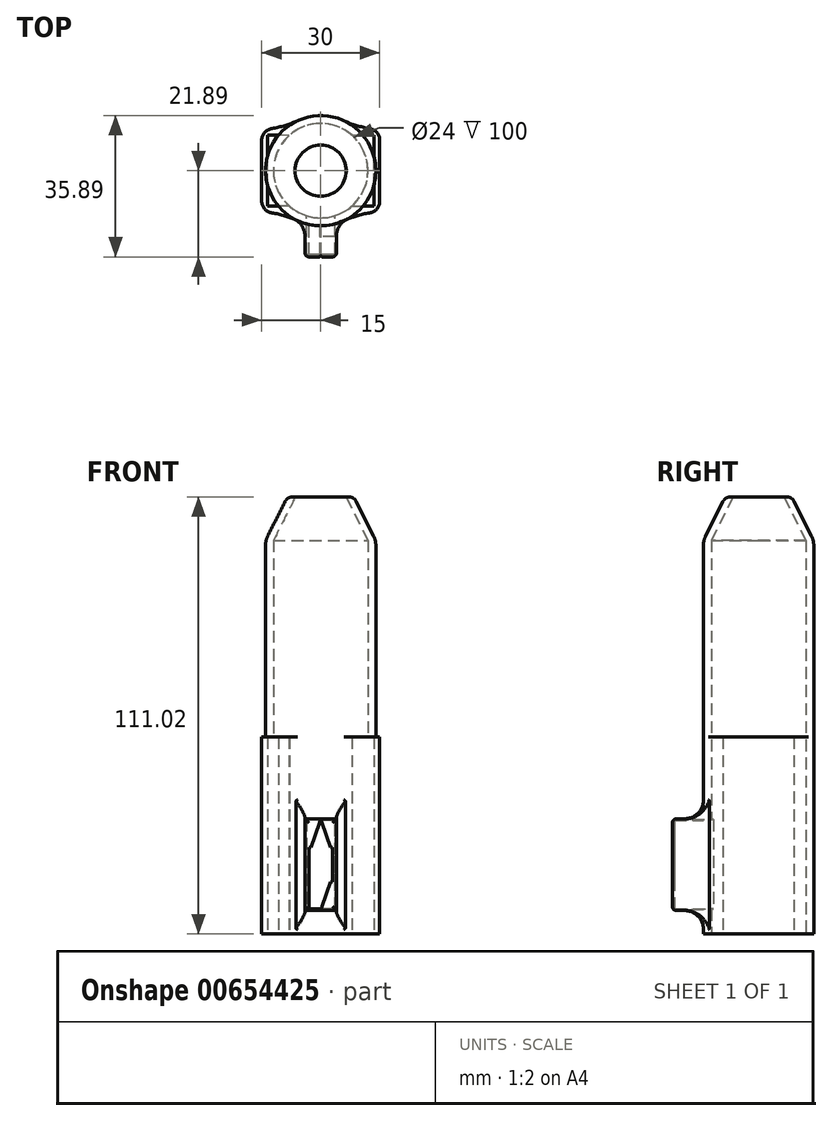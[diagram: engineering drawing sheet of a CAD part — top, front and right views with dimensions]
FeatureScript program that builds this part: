
annotation { "Feature Type Name" : "Feature", "Feature Type Description" : "" }
export const myFeature = defineFeature(function(context is Context, id is Id, definition is map)
    precondition{}
    {
        {
            var Q0;
            Q0=qCreatedBy(makeId("Front.planeOp"),FACE);
            var sketch = newSketch(context, id + "F0", { "sketchPlane" : qUnion([Q0])});
            skLineSegment(sketch, "E0", {"start": v(-12, -57.81) * mm, "end": v(-12, 40.19) * mm});
            skLineSegment(sketch, "E1", {"start": v(-12, 40.19) * mm, "end": v(-14, 40.19) * mm});
            skLineSegment(sketch, "E2", {"start": v(-14, 40.19) * mm, "end": v(-14, -59.81) * mm});
            skLineSegment(sketch, "E3", {"start": v(0, -59.81) * mm, "end": v(0, -57.81) * mm});
            skLineSegment(sketch, "E4", {"start": v(-12, 40.19) * mm, "end": v(-6.5, 51.08) * mm});
            skLineSegment(sketch, "E5", {"start": v(-14, 40.19) * mm, "end": v(-6.5, 55.08) * mm});
            skLineSegment(sketch, "E6", {"start": v(-6.5, 55.08) * mm, "end": v(-6.5, 51.08) * mm});
            skLineSegment(sketch, "E7", {"start": v(-12, -57.81) * mm, "end": v(-12, -59.81) * mm});
            skLineSegment(sketch, "E8", {"start": v(-12, -59.81) * mm, "end": v(-14, -59.81) * mm});
            skSolve(sketch);
        }
        {
            var Q0;
            Q0 = qSketchRegion(id + "F0", true);
            var Q1;
            Q1=sQuery(id+"F0.wireOp",EDGE,"E3");
            revolve(context, id + "F1", {"entities" : qUnion([Q0]), "axis" : qUnion([Q1]), "revolveType" : RevolveType.FULL});
        }
        {
            var Q0;
            Q0=makeQuery(id+"F1.opRevolve","SWEPT_EDGE",EDGE,{"disambiguationData":[OSD([sQuery(id+"F0.wireOp",EDGE,"E5"),sQuery(id+"F0.wireOp",EDGE,"E6")])]});
            fillet(context, id + "F2", {"entities" : qUnion([Q0]), "radius" : 2 * mm, "tangentPropagation" : true, "allowEdgeOverflow" : false});
        }
        {
            var Q0;
            Q0=makeQuery(id+"F1.opRevolve","SWEPT_EDGE",EDGE,{"disambiguationData":[OSD([sQuery(id+"F0.wireOp",EDGE,"E1"),sQuery(id+"F0.wireOp",EDGE,"E2"),sQuery(id+"F0.wireOp",EDGE,"E5")])]});
            fillet(context, id + "F3", {"entities" : qUnion([Q0]), "radius" : 5 * mm, "tangentPropagation" : true, "allowEdgeOverflow" : false});
        }
        {
            var Q0;
            Q0=qCreatedBy(makeId("Front.planeOp"),FACE);
            var sketch = newSketch(context, id + "F4", { "sketchPlane" : qUnion([Q0])});
            skLineSegment(sketch, "E9.bottom", {"start": v(4, -30.57) * mm, "end": v(-4, -30.57) * mm});
            skLineSegment(sketch, "E9.top", {"start": v(4, -53.87) * mm, "end": v(-4, -53.87) * mm});
            skLineSegment(sketch, "E9.left", {"start": v(4, -30.57) * mm, "end": v(4, -53.87) * mm});
            skLineSegment(sketch, "E9.right", {"start": v(-4, -30.57) * mm, "end": v(-4, -53.87) * mm});
            skLineSegment(sketch, "E10", {"start": v(-4, -30.57) * mm, "end": v(-3, -30.57) * mm});
            skLineSegment(sketch, "E11", {"start": v(4, -30.57) * mm, "end": v(3, -30.57) * mm});
            skLineSegment(sketch, "E12", {"start": v(3, -30.57) * mm, "end": v(3, -53.87) * mm});
            skLineSegment(sketch, "E13", {"start": v(-3, -30.57) * mm, "end": v(-3, -53.87) * mm});
            skLineSegment(sketch, "E14", {"start": v(0, -30.57) * mm, "end": v(-2.5, -37.87) * mm});
            skLineSegment(sketch, "E15", {"start": v(-2.5, -37.87) * mm, "end": v(-3, -37.87) * mm});
            skLineSegment(sketch, "E16", {"start": v(3, -37.87) * mm, "end": v(2.5, -37.87) * mm});
            skLineSegment(sketch, "E17", {"start": v(0, -30.57) * mm, "end": v(2.5, -37.87) * mm});
            skLineSegment(sketch, "E18", {"start": v(3, -46.57) * mm, "end": v(2.5, -46.57) * mm});
            skLineSegment(sketch, "E19", {"start": v(2.5, -46.57) * mm, "end": v(0, -53.87) * mm});
            skLineSegment(sketch, "E20", {"start": v(-3, -46.57) * mm, "end": v(-2.5, -46.57) * mm});
            skLineSegment(sketch, "E21", {"start": v(-2.5, -46.57) * mm, "end": v(0, -53.87) * mm});
            skLineSegment(sketch, "E22", {"start": v(-2.5, -46.57) * mm, "end": v(-3, -46.57) * mm});
            skLineSegment(sketch, "E23", {"start": v(-0.12, -30.9) * mm, "end": v(0, -30.87) * mm});
            skLineSegment(sketch, "E24", {"start": v(-0.1, -53.56) * mm, "end": v(0.14, -53.47) * mm});
            skLineSegment(sketch, "E25", {"start": v(-3, -30.84) * mm, "end": v(3, -30.84) * mm});
            skLineSegment(sketch, "E26", {"start": v(-3, -53.57) * mm, "end": v(3, -53.57) * mm});
            skSolve(sketch);
        }
        {
            var Q0;
            Q0 = qSketchRegion(id + "F4", true);
            var Q1;
            {var subQ4=sQuery(id+"F4.wireOp",EDGE,"E18");Q1=makeQuery(id+"F4.imprint","IMPRINT",FACE,{"disambiguationData":[TD([[makeQuery(id+"F4.imprint","IMPRINT",EDGE,{"derivedFrom":subQ4}),1.0]])]});}
            var Q2;
            {var subQ0=sQuery(id+"F4.wireOp",EDGE,"E22");Q2=makeQuery(id+"F4.imprint","IMPRINT",FACE,{"disambiguationData":[TD([[makeQuery(id+"F4.imprint","IMPRINT",EDGE,{"derivedFrom":subQ0}),1.0]])]});}
            var Q3;
            {var subQ0=sQuery(id+"F4.wireOp",EDGE,"E15");Q3=makeQuery(id+"F4.imprint","IMPRINT",FACE,{"disambiguationData":[TD([[makeQuery(id+"F4.imprint","IMPRINT",EDGE,{"derivedFrom":subQ0}),-1.0]])]});}
            var Q4;
            {var subQ0=sQuery(id+"F4.wireOp",EDGE,"E16");Q4=makeQuery(id+"F4.imprint","IMPRINT",FACE,{"disambiguationData":[TD([[makeQuery(id+"F4.imprint","IMPRINT",EDGE,{"derivedFrom":subQ0}),-1.0]])]});}
            extrude(context, id + "F5", {"entities" : qUnion([Q0, Q1, Q2, Q3, Q4]), "operationType" : NewBodyOperationType.ADD, "depth" : 17.79 * mm, "offsetDistance" : 25 * mm});
        }
        {
            var Q0;
            Q0=makeQuery(id+"F5.opExtrude","CAP_FACE",FACE,{"disambiguationData":[OSD([sQuery(id+"F4.wireOp",EDGE,"E9.bottom"),sQuery(id+"F4.wireOp",EDGE,"E9.top"),sQuery(id+"F4.wireOp",EDGE,"E9.left"),sQuery(id+"F4.wireOp",EDGE,"E9.right"),sQuery(id+"F4.wireOp",EDGE,"E10"),sQuery(id+"F4.wireOp",EDGE,"E11"),sQuery(id+"F4.wireOp",EDGE,"E12"),sQuery(id+"F4.wireOp",EDGE,"E13"),sQuery(id+"F4.wireOp",EDGE,"E14"),sQuery(id+"F4.wireOp",EDGE,"E15"),sQuery(id+"F4.wireOp",EDGE,"E16"),sQuery(id+"F4.wireOp",EDGE,"E17"),sQuery(id+"F4.wireOp",EDGE,"E18"),sQuery(id+"F4.wireOp",EDGE,"E19"),sQuery(id+"F4.wireOp",EDGE,"E21"),sQuery(id+"F4.wireOp",EDGE,"E22"),sQuery(id+"F4.wireOp",EDGE,"E25"),sQuery(id+"F4.wireOp",EDGE,"E26")])],"isStart":true});
            var sketch = newSketch(context, id + "F6", { "sketchPlane" : qUnion([Q0])});
            skSolve(sketch);
        }
        {
            var Q0;
            Q0=makeQuery(id+"F6.imprint","IMPRINT",FACE,{"disambiguationData":[TD([[makeQuery(id+"F6.imprint","IMPRINT",EDGE,{"derivedFrom":makeQuery(id+"F5.opExtrude","CAP_EDGE",EDGE,{"disambiguationData":[OSD([sQuery(id+"F4.wireOp",EDGE,"E9.top")])],"isStart":true})}),1.0]])]});
            var sketch = newSketch(context, id + "F7", { "sketchPlane" : qUnion([Q0])});
            skLineSegment(sketch, "E27.bottom", {"start": v(-3.6, -53.47) * mm, "end": v(3.6, -53.47) * mm});
            skLineSegment(sketch, "E27.top", {"start": v(-3.6, -30.97) * mm, "end": v(3.6, -30.97) * mm});
            skLineSegment(sketch, "E27.left", {"start": v(-3.6, -53.47) * mm, "end": v(-3.6, -30.97) * mm});
            skLineSegment(sketch, "E27.right", {"start": v(3.6, -53.47) * mm, "end": v(3.6, -30.97) * mm});
            skSolve(sketch);
        }
        {
            var Q0;
            Q0 = qSketchRegion(id + "F7", true);
            extrude(context, id + "F8", {"entities" : qUnion([Q0]), "operationType" : NewBodyOperationType.REMOVE, "oppositeDirection" : true, "depth" : 16.7 * mm, "offsetDistance" : 25 * mm});
        }
        {
            var Q0;
            {var subQ2=sQuery(id+"F4.wireOp",EDGE,"E9.top");Q0=makeQuery(id+"F5.boolean.opBoolean","SPLIT",FACE,{"disambiguationData":[TD([makeQuery(id+"F1.opRevolve","SWEPT_FACE",FACE,{"disambiguationData":[OSD([sQuery(id+"F0.wireOp",EDGE,"E0"),sQuery(id+"F0.wireOp",EDGE,"E7")])]})])],"derivedFrom":makeQuery(id+"F5.opExtrude","SWEPT_FACE",FACE,{"disambiguationData":[OSD([subQ2])]})});}
            extrude(context, id + "F9", {"entities" : qUnion([Q0]), "operationType" : NewBodyOperationType.REMOVE, "oppositeDirection" : true, "depth" : 25 * mm, "offsetDistance" : 25 * mm});
        }
        {
            var Q0;
            {var subQ0=sQuery(id+"F7.wireOp",EDGE,"E27.left");var subQ1=sQuery(id+"F7.wireOp",EDGE,"E27.bottom");var subQ2=sQuery(id+"F7.wireOp",EDGE,"E27.top");Q0=makeQuery(id+"F8.boolean.opBoolean","COPY",FACE,{"disambiguationData":[TD([makeQuery(id+"F5.opExtrude","SWEPT_FACE",FACE,{"disambiguationData":[OSD([sQuery(id+"F4.wireOp",EDGE,"E12")])]})])],"derivedFrom":makeQuery(id+"F8.opExtrude","CAP_FACE",FACE,{"disambiguationData":[OSD([subQ1,subQ2,subQ0,sQuery(id+"F7.wireOp",EDGE,"E27.right")])],"isStart":false})});}
            var sketch = newSketch(context, id + "F10", { "sketchPlane" : qUnion([Q0])});
            skLineSegment(sketch, "E28", {"start": v(-3.6, -53.47) * mm, "end": v(-3.6, -30.97) * mm});
            skSolve(sketch);
        }
        {
            var Q0;
            Q0=makeQuery(id+"F8.boolean.opBoolean","COPY",FACE,{"derivedFrom":makeQuery(id+"F8.opExtrude","SWEPT_FACE",FACE,{"disambiguationData":[OSD([sQuery(id+"F7.wireOp",EDGE,"E27.top")])]})});
            extrude(context, id + "F11", {"entities" : qUnion([Q0]), "operationType" : NewBodyOperationType.REMOVE, "oppositeDirection" : true, "depth" : 0.19 * mm, "offsetDistance" : 25 * mm});
        }
        {
            var Q0;
            Q0=makeQuery(id+"F1.opRevolve","SWEPT_FACE",FACE,{"disambiguationData":[OSD([sQuery(id+"F0.wireOp",EDGE,"E8")])]});
            var sketch = newSketch(context, id + "F12", { "sketchPlane" : qUnion([Q0])});
            skLineSegment(sketch, "E29", {"start": v(13.5, 0) * mm, "end": v(13.5, -9) * mm});
            skLineSegment(sketch, "E30", {"start": v(13.5, 0) * mm, "end": v(13.5, 9) * mm});
            skLineSegment(sketch, "E31", {"start": v(-13.5, 9) * mm, "end": v(-13.5, 0) * mm});
            skLineSegment(sketch, "E32", {"start": v(-13.5, -9) * mm, "end": v(-13.5, 0) * mm});
            skLineSegment(sketch, "E33", {"start": v(13.5, 9) * mm, "end": v(15, 9) * mm});
            skLineSegment(sketch, "E34", {"start": v(13.5, -9) * mm, "end": v(15, -9) * mm});
            skLineSegment(sketch, "E35", {"start": v(15, 9) * mm, "end": v(15, -9) * mm});
            skLineSegment(sketch, "E36", {"start": v(13.5, 9) * mm, "end": v(13.5, 10.5) * mm});
            skLineSegment(sketch, "E37", {"start": v(13.5, -9) * mm, "end": v(13.5, -10.5) * mm});
            skLineSegment(sketch, "E38", {"start": v(-13.5, -9) * mm, "end": v(-13.5, -10.5) * mm});
            skLineSegment(sketch, "E39", {"start": v(-13.5, -9) * mm, "end": v(-15, -9) * mm});
            skLineSegment(sketch, "E40", {"start": v(-14, 0) * mm, "end": v(-13.5, 0) * mm});
            skLineSegment(sketch, "E41", {"start": v(13.5, 0) * mm, "end": v(14, 0) * mm});
            skLineSegment(sketch, "E42", {"start": v(-13.5, 9) * mm, "end": v(-13.5, 10.5) * mm});
            skLineSegment(sketch, "E43", {"start": v(-13.5, 9) * mm, "end": v(-15, 9) * mm});
            skLineSegment(sketch, "E44", {"start": v(-15, 9) * mm, "end": v(-15, -10.5) * mm});
            skLineSegment(sketch, "E45", {"start": v(15, -10.5) * mm, "end": v(15, 10.5) * mm});
            skLineSegment(sketch, "E46", {"start": v(-15, 9) * mm, "end": v(-15, 10.5) * mm});
            skLineSegment(sketch, "E47", {"start": v(-15, 10.5) * mm, "end": v(-13.5, 10.5) * mm});
            skLineSegment(sketch, "E48", {"start": v(9.56, 9) * mm, "end": v(7.85, 10.5) * mm});
            skLineSegment(sketch, "E49", {"start": v(-7.61, 10.5) * mm, "end": v(-9.13, 9) * mm});
            skLineSegment(sketch, "E50", {"start": v(-9.13, 9) * mm, "end": v(-13.5, 9) * mm});
            skLineSegment(sketch, "E51", {"start": v(9.56, 9) * mm, "end": v(13.5, 9) * mm});
            skLineSegment(sketch, "E52", {"start": v(7.85, 10.5) * mm, "end": v(13.5, 10.5) * mm});
            skLineSegment(sketch, "E53", {"start": v(-7.61, 10.5) * mm, "end": v(-13.5, 10.5) * mm});
            skLineSegment(sketch, "E54", {"start": v(13.5, 10.5) * mm, "end": v(15, 10.5) * mm});
            skLineSegment(sketch, "E55", {"start": v(-7.73, -10.5) * mm, "end": v(-8.96, -9) * mm});
            skLineSegment(sketch, "E56", {"start": v(9.29, -9) * mm, "end": v(7.83, -10.5) * mm});
            skLineSegment(sketch, "E57", {"start": v(7.83, -10.5) * mm, "end": v(15, -10.5) * mm});
            skLineSegment(sketch, "E58", {"start": v(-7.73, -10.5) * mm, "end": v(-15, -10.5) * mm});
            skLineSegment(sketch, "E59", {"start": v(9.29, -9) * mm, "end": v(13.5, -9) * mm});
            skLineSegment(sketch, "E60", {"start": v(-8.96, -9) * mm, "end": v(-13.5, -9) * mm});
            skSolve(sketch);
        }
        {
            var Q0;
            Q0 = qSketchRegion(id + "F12", true);
            extrude(context, id + "F13", {"entities" : qUnion([Q0]), "operationType" : NewBodyOperationType.ADD, "oppositeDirection" : true, "depth" : 50 * mm, "offsetDistance" : 25 * mm});
        }
        {
            var Q0;
            Q0=makeQuery(id+"F13.boolean.opBoolean","MERGE",FACE,{"derivedFrom":[makeQuery(id+"F1.opRevolve","SWEPT_FACE",FACE,{"disambiguationData":[OSD([sQuery(id+"F0.wireOp",EDGE,"E8")])]}),makeQuery(id+"F13.opExtrude","CAP_FACE",FACE,{"disambiguationData":[OSD([sQuery(id+"F12.wireOp",EDGE,"E29"),sQuery(id+"F12.wireOp",EDGE,"E30"),sQuery(id+"F12.wireOp",EDGE,"E45"),sQuery(id+"F12.wireOp",EDGE,"E48"),sQuery(id+"F12.wireOp",EDGE,"E51"),sQuery(id+"F12.wireOp",EDGE,"E52"),sQuery(id+"F12.wireOp",EDGE,"E54"),sQuery(id+"F12.wireOp",EDGE,"E56"),sQuery(id+"F12.wireOp",EDGE,"E57"),sQuery(id+"F12.wireOp",EDGE,"E59")])],"isStart":true}),makeQuery(id+"F13.opExtrude","CAP_FACE",FACE,{"disambiguationData":[OSD([sQuery(id+"F12.wireOp",EDGE,"E31"),sQuery(id+"F12.wireOp",EDGE,"E32"),sQuery(id+"F12.wireOp",EDGE,"E44"),sQuery(id+"F12.wireOp",EDGE,"E46"),sQuery(id+"F12.wireOp",EDGE,"E47"),sQuery(id+"F12.wireOp",EDGE,"E49"),sQuery(id+"F12.wireOp",EDGE,"E50"),sQuery(id+"F12.wireOp",EDGE,"E53"),sQuery(id+"F12.wireOp",EDGE,"E55"),sQuery(id+"F12.wireOp",EDGE,"E58"),sQuery(id+"F12.wireOp",EDGE,"E60")])],"isStart":true})]});
            var sketch = newSketch(context, id + "F14", { "sketchPlane" : qUnion([Q0])});
            skLineSegment(sketch, "E61", {"start": v(10.72, 9) * mm, "end": v(7.94, 9) * mm});
            skLineSegment(sketch, "E62", {"start": v(7.94, 9) * mm, "end": v(7.94, 3.7) * mm});
            skLineSegment(sketch, "E63", {"start": v(7.94, 3.7) * mm, "end": v(13.5, 3.7) * mm});
            skLineSegment(sketch, "E64", {"start": v(13.5, -3.7) * mm, "end": v(8.05, -3.7) * mm});
            skLineSegment(sketch, "E65", {"start": v(8.05, -3.7) * mm, "end": v(7.49, -3.7) * mm});
            skLineSegment(sketch, "E66", {"start": v(7.49, -3.7) * mm, "end": v(7.49, -9) * mm});
            skLineSegment(sketch, "E67", {"start": v(7.49, -9) * mm, "end": v(10.72, -9) * mm});
            skLineSegment(sketch, "E68", {"start": v(-13.5, -3.7) * mm, "end": v(-6.61, -3.7) * mm});
            skLineSegment(sketch, "E69", {"start": v(-6.61, -3.7) * mm, "end": v(-6.61, -8.93) * mm});
            skLineSegment(sketch, "E70", {"start": v(-6.61, -8.93) * mm, "end": v(-10.72, -9) * mm});
            skLineSegment(sketch, "E71", {"start": v(-10.72, -9) * mm, "end": v(-13.5, -9) * mm});
            skLineSegment(sketch, "E72", {"start": v(-13.5, -9) * mm, "end": v(-13.5, -3.7) * mm});
            skLineSegment(sketch, "E73", {"start": v(10.72, -9) * mm, "end": v(13.5, -9) * mm});
            skLineSegment(sketch, "E74", {"start": v(13.5, -9) * mm, "end": v(13.5, -3.7) * mm});
            skLineSegment(sketch, "E75", {"start": v(10.72, 9) * mm, "end": v(13.5, 9) * mm});
            skLineSegment(sketch, "E76", {"start": v(13.5, 9) * mm, "end": v(13.5, 3.7) * mm});
            skLineSegment(sketch, "E77", {"start": v(-13.5, 9) * mm, "end": v(-4.7, 9) * mm});
            skLineSegment(sketch, "E78", {"start": v(-4.7, 9) * mm, "end": v(-4.6, 3.7) * mm});
            skLineSegment(sketch, "E79", {"start": v(-4.6, 3.7) * mm, "end": v(-13.5, 3.7) * mm});
            skLineSegment(sketch, "E80", {"start": v(-13.5, 3.7) * mm, "end": v(-13.5, 9) * mm});
            skSolve(sketch);
        }
        {
            var Q0;
            Q0 = qSketchRegion(id + "F14", true);
            extrude(context, id + "F15", {"entities" : qUnion([Q0]), "operationType" : NewBodyOperationType.REMOVE, "oppositeDirection" : true, "depth" : 50 * mm, "offsetDistance" : 25 * mm});
        }
        {
            var Q0;
            Q0=makeQuery(id+"F13.boolean.opBoolean","MERGE",FACE,{"derivedFrom":[makeQuery(id+"F1.opRevolve","SWEPT_FACE",FACE,{"disambiguationData":[OSD([sQuery(id+"F0.wireOp",EDGE,"E8")])]}),makeQuery(id+"F13.opExtrude","CAP_FACE",FACE,{"disambiguationData":[OSD([sQuery(id+"F12.wireOp",EDGE,"E29"),sQuery(id+"F12.wireOp",EDGE,"E30"),sQuery(id+"F12.wireOp",EDGE,"E45"),sQuery(id+"F12.wireOp",EDGE,"E48"),sQuery(id+"F12.wireOp",EDGE,"E51"),sQuery(id+"F12.wireOp",EDGE,"E52"),sQuery(id+"F12.wireOp",EDGE,"E54"),sQuery(id+"F12.wireOp",EDGE,"E56"),sQuery(id+"F12.wireOp",EDGE,"E57"),sQuery(id+"F12.wireOp",EDGE,"E59")])],"isStart":true}),makeQuery(id+"F13.opExtrude","CAP_FACE",FACE,{"disambiguationData":[OSD([sQuery(id+"F12.wireOp",EDGE,"E31"),sQuery(id+"F12.wireOp",EDGE,"E32"),sQuery(id+"F12.wireOp",EDGE,"E44"),sQuery(id+"F12.wireOp",EDGE,"E46"),sQuery(id+"F12.wireOp",EDGE,"E47"),sQuery(id+"F12.wireOp",EDGE,"E49"),sQuery(id+"F12.wireOp",EDGE,"E50"),sQuery(id+"F12.wireOp",EDGE,"E53"),sQuery(id+"F12.wireOp",EDGE,"E55"),sQuery(id+"F12.wireOp",EDGE,"E58"),sQuery(id+"F12.wireOp",EDGE,"E60")])],"isStart":true})]});
            var sketch = newSketch(context, id + "F16", { "sketchPlane" : qUnion([Q0])});
            skLineSegment(sketch, "E81", {"start": v(13.5, 3.7) * mm, "end": v(13.5, -3.7) * mm});
            skLineSegment(sketch, "E82", {"start": v(13.5, -3.7) * mm, "end": v(8.2, -3.7) * mm});
            skLineSegment(sketch, "E83", {"start": v(8.2, -3.7) * mm, "end": v(8.2, 3.7) * mm});
            skLineSegment(sketch, "E84", {"start": v(8.2, 3.7) * mm, "end": v(13.5, 3.7) * mm});
            skLineSegment(sketch, "E85", {"start": v(-13.5, 3.7) * mm, "end": v(-13.5, -3.7) * mm});
            skLineSegment(sketch, "E86", {"start": v(-13.5, -3.7) * mm, "end": v(-6.7, -3.7) * mm});
            skLineSegment(sketch, "E87", {"start": v(-6.7, -3.7) * mm, "end": v(-6.7, 3.7) * mm});
            skLineSegment(sketch, "E88", {"start": v(-6.7, 3.7) * mm, "end": v(-13.5, 3.7) * mm});
            skSolve(sketch);
        }
        {
            var Q0;
            Q0 = qSketchRegion(id + "F16", true);
            extrude(context, id + "F17", {"entities" : qUnion([Q0]), "operationType" : NewBodyOperationType.REMOVE, "oppositeDirection" : true, "depth" : 50 * mm, "offsetDistance" : 25 * mm});
        }
        {
            var Q0;
            Q0=makeQuery(id+"F5.opExtrude","CAP_FACE",FACE,{"disambiguationData":[OSD([sQuery(id+"F4.wireOp",EDGE,"E9.bottom"),sQuery(id+"F4.wireOp",EDGE,"E9.top"),sQuery(id+"F4.wireOp",EDGE,"E9.left"),sQuery(id+"F4.wireOp",EDGE,"E9.right"),sQuery(id+"F4.wireOp",EDGE,"E10"),sQuery(id+"F4.wireOp",EDGE,"E11"),sQuery(id+"F4.wireOp",EDGE,"E12"),sQuery(id+"F4.wireOp",EDGE,"E13"),sQuery(id+"F4.wireOp",EDGE,"E14"),sQuery(id+"F4.wireOp",EDGE,"E15"),sQuery(id+"F4.wireOp",EDGE,"E16"),sQuery(id+"F4.wireOp",EDGE,"E17"),sQuery(id+"F4.wireOp",EDGE,"E18"),sQuery(id+"F4.wireOp",EDGE,"E19"),sQuery(id+"F4.wireOp",EDGE,"E21"),sQuery(id+"F4.wireOp",EDGE,"E22"),sQuery(id+"F4.wireOp",EDGE,"E25"),sQuery(id+"F4.wireOp",EDGE,"E26")])],"isStart":false});
            extrude(context, id + "F18", {"entities" : qUnion([Q0]), "operationType" : NewBodyOperationType.ADD, "depth" : 4.1 * mm, "offsetDistance" : 25 * mm});
        }
        {
            var Q0;
            Q0=makeQuery(id+"F10.imprint","IMPRINT",FACE,{"disambiguationData":[TD([[makeQuery(id+"F10.imprint","IMPRINT",EDGE,{"derivedFrom":sQuery(id+"F10.wireOp",EDGE,"E28")}),-1.0]])]});
            extrude(context, id + "F19", {"entities" : qUnion([Q0]), "operationType" : NewBodyOperationType.REMOVE, "oppositeDirection" : true, "depth" : 4.6 * mm, "offsetDistance" : 25 * mm});
        }
        {
            var Q0;
            {var subQ0=makeQuery(id+"F5.opExtrude","SWEPT_FACE",FACE,{"disambiguationData":[OSD([sQuery(id+"F4.wireOp",EDGE,"E14")])]});var subQ1=sQuery(id+"F7.wireOp",EDGE,"E27.right");var subQ2=sQuery(id+"F7.wireOp",EDGE,"E27.top");var subQ3=sQuery(id+"F7.wireOp",EDGE,"E27.bottom");var subQ4=makeQuery(id+"F8.opExtrude","CAP_FACE",FACE,{"disambiguationData":[OSD([subQ3,subQ2,sQuery(id+"F7.wireOp",EDGE,"E27.left"),subQ1])],"isStart":false});Q0=makeQuery(id+"F11.boolean.opBoolean","MERGE",FACE,{"derivedFrom":[makeQuery(id+"F8.boolean.opBoolean","COPY",FACE,{"disambiguationData":[TD([makeQuery(id+"F5.opExtrude","SWEPT_FACE",FACE,{"disambiguationData":[OSD([sQuery(id+"F4.wireOp",EDGE,"E13")])]})])],"derivedFrom":subQ4}),makeQuery(id+"F11.opExtrude","SWEPT_FACE",FACE,{"disambiguationData":[OSD([subQ2]),TDD([makeQuery(id+"F8.boolean.opBoolean","COPY",EDGE,{"disambiguationData":[TD([subQ0])],"derivedFrom":makeQuery(id+"F8.opExtrude","CAP_EDGE",EDGE,{"disambiguationData":[OSD([subQ2])],"isStart":false})})])]})]});}
            extrude(context, id + "F20", {"entities" : qUnion([Q0]), "operationType" : NewBodyOperationType.REMOVE, "oppositeDirection" : true, "depth" : 4.6 * mm, "offsetDistance" : 25 * mm});
        }
        {
            var Q0;
            {var subQ0=sQuery(id+"F0.wireOp",EDGE,"E2");Q0=makeQuery(id+"F13.boolean.opBoolean","INTERSECT",EDGE,{"derivedFrom":[makeQuery(id+"F5.boolean.opBoolean","SPLIT",FACE,{"disambiguationData":[TD([makeQuery(id+"F1.opRevolve","SWEPT_FACE",FACE,{"disambiguationData":[OSD([sQuery(id+"F0.wireOp",EDGE,"E8")])]})])],"derivedFrom":makeQuery(id+"F1.opRevolve","SWEPT_FACE",FACE,{"disambiguationData":[OSD([subQ0])]})}),makeQuery(id+"F13.opExtrude","SWEPT_FACE",FACE,{"disambiguationData":[OSD([sQuery(id+"F12.wireOp",EDGE,"E52"),sQuery(id+"F12.wireOp",EDGE,"E54")])]})]});}
            var Q1;
            {var subQ0=sQuery(id+"F0.wireOp",EDGE,"E2");Q1=makeQuery(id+"F13.boolean.opBoolean","INTERSECT",EDGE,{"derivedFrom":[makeQuery(id+"F5.boolean.opBoolean","SPLIT",FACE,{"disambiguationData":[TD([makeQuery(id+"F1.opRevolve","SWEPT_FACE",FACE,{"disambiguationData":[OSD([sQuery(id+"F0.wireOp",EDGE,"E8")])]})])],"derivedFrom":makeQuery(id+"F1.opRevolve","SWEPT_FACE",FACE,{"disambiguationData":[OSD([subQ0])]})}),makeQuery(id+"F13.opExtrude","SWEPT_FACE",FACE,{"disambiguationData":[OSD([sQuery(id+"F12.wireOp",EDGE,"E47"),sQuery(id+"F12.wireOp",EDGE,"E53")])]})]});}
            var Q2;
            {var subQ0=sQuery(id+"F0.wireOp",EDGE,"E2");Q2=makeQuery(id+"F13.boolean.opBoolean","INTERSECT",EDGE,{"derivedFrom":[makeQuery(id+"F5.boolean.opBoolean","SPLIT",FACE,{"disambiguationData":[TD([makeQuery(id+"F1.opRevolve","SWEPT_FACE",FACE,{"disambiguationData":[OSD([sQuery(id+"F0.wireOp",EDGE,"E8")])]})])],"derivedFrom":makeQuery(id+"F1.opRevolve","SWEPT_FACE",FACE,{"disambiguationData":[OSD([subQ0])]})}),makeQuery(id+"F13.opExtrude","SWEPT_FACE",FACE,{"disambiguationData":[OSD([sQuery(id+"F12.wireOp",EDGE,"E57")])]})]});}
            var Q3;
            {var subQ0=sQuery(id+"F0.wireOp",EDGE,"E2");Q3=makeQuery(id+"F13.boolean.opBoolean","INTERSECT",EDGE,{"derivedFrom":[makeQuery(id+"F5.boolean.opBoolean","SPLIT",FACE,{"disambiguationData":[TD([makeQuery(id+"F1.opRevolve","SWEPT_FACE",FACE,{"disambiguationData":[OSD([sQuery(id+"F0.wireOp",EDGE,"E8")])]})])],"derivedFrom":makeQuery(id+"F1.opRevolve","SWEPT_FACE",FACE,{"disambiguationData":[OSD([subQ0])]})}),makeQuery(id+"F13.opExtrude","SWEPT_FACE",FACE,{"disambiguationData":[OSD([sQuery(id+"F12.wireOp",EDGE,"E58")])]})]});}
            fillet(context, id + "F21", {"entities" : qUnion([Q0, Q1, Q2, Q3]), "radius" : 23.17 * mm, "tangentPropagation" : true, "allowEdgeOverflow" : false});
        }
        {
            var Q0;
            {var subQ0=sQuery(id+"F0.wireOp",EDGE,"E2");Q0=makeQuery(id+"F21.opFillet","BLEND_EDGE",EDGE,{"blendedFrom":[makeQuery(id+"F13.boolean.opBoolean","INTERSECT",EDGE,{"derivedFrom":[makeQuery(id+"F5.boolean.opBoolean","SPLIT",FACE,{"disambiguationData":[TD([makeQuery(id+"F1.opRevolve","SWEPT_FACE",FACE,{"disambiguationData":[OSD([sQuery(id+"F0.wireOp",EDGE,"E8")])]})])],"derivedFrom":makeQuery(id+"F1.opRevolve","SWEPT_FACE",FACE,{"disambiguationData":[OSD([subQ0])]})}),makeQuery(id+"F13.opExtrude","SWEPT_FACE",FACE,{"disambiguationData":[OSD([sQuery(id+"F12.wireOp",EDGE,"E47"),sQuery(id+"F12.wireOp",EDGE,"E53")])]})]}),makeQuery(id+"F13.opExtrude","SWEPT_FACE",FACE,{"disambiguationData":[OSD([sQuery(id+"F12.wireOp",EDGE,"E44"),sQuery(id+"F12.wireOp",EDGE,"E46")])]})],"blendedInto":[makeQuery(id+"F13.opExtrude","SWEPT_FACE",FACE,{"disambiguationData":[OSD([sQuery(id+"F12.wireOp",EDGE,"E44"),sQuery(id+"F12.wireOp",EDGE,"E46")])]})]});}
            var Q1;
            {var subQ0=sQuery(id+"F0.wireOp",EDGE,"E2");Q1=makeQuery(id+"F21.opFillet","BLEND_EDGE",EDGE,{"blendedFrom":[makeQuery(id+"F13.boolean.opBoolean","INTERSECT",EDGE,{"derivedFrom":[makeQuery(id+"F5.boolean.opBoolean","SPLIT",FACE,{"disambiguationData":[TD([makeQuery(id+"F1.opRevolve","SWEPT_FACE",FACE,{"disambiguationData":[OSD([sQuery(id+"F0.wireOp",EDGE,"E8")])]})])],"derivedFrom":makeQuery(id+"F1.opRevolve","SWEPT_FACE",FACE,{"disambiguationData":[OSD([subQ0])]})}),makeQuery(id+"F13.opExtrude","SWEPT_FACE",FACE,{"disambiguationData":[OSD([sQuery(id+"F12.wireOp",EDGE,"E58")])]})]}),makeQuery(id+"F13.opExtrude","SWEPT_FACE",FACE,{"disambiguationData":[OSD([sQuery(id+"F12.wireOp",EDGE,"E44"),sQuery(id+"F12.wireOp",EDGE,"E46")])]})],"blendedInto":[makeQuery(id+"F13.opExtrude","SWEPT_FACE",FACE,{"disambiguationData":[OSD([sQuery(id+"F12.wireOp",EDGE,"E44"),sQuery(id+"F12.wireOp",EDGE,"E46")])]})]});}
            var Q2;
            {var subQ0=sQuery(id+"F0.wireOp",EDGE,"E2");Q2=makeQuery(id+"F21.opFillet","BLEND_EDGE",EDGE,{"blendedFrom":[makeQuery(id+"F13.boolean.opBoolean","INTERSECT",EDGE,{"derivedFrom":[makeQuery(id+"F5.boolean.opBoolean","SPLIT",FACE,{"disambiguationData":[TD([makeQuery(id+"F1.opRevolve","SWEPT_FACE",FACE,{"disambiguationData":[OSD([sQuery(id+"F0.wireOp",EDGE,"E8")])]})])],"derivedFrom":makeQuery(id+"F1.opRevolve","SWEPT_FACE",FACE,{"disambiguationData":[OSD([subQ0])]})}),makeQuery(id+"F13.opExtrude","SWEPT_FACE",FACE,{"disambiguationData":[OSD([sQuery(id+"F12.wireOp",EDGE,"E57")])]})]}),makeQuery(id+"F13.opExtrude","SWEPT_FACE",FACE,{"disambiguationData":[OSD([sQuery(id+"F12.wireOp",EDGE,"E45")])]})],"blendedInto":[makeQuery(id+"F13.opExtrude","SWEPT_FACE",FACE,{"disambiguationData":[OSD([sQuery(id+"F12.wireOp",EDGE,"E45")])]})]});}
            var Q3;
            {var subQ0=sQuery(id+"F0.wireOp",EDGE,"E2");Q3=makeQuery(id+"F21.opFillet","BLEND_EDGE",EDGE,{"blendedFrom":[makeQuery(id+"F13.boolean.opBoolean","INTERSECT",EDGE,{"derivedFrom":[makeQuery(id+"F5.boolean.opBoolean","SPLIT",FACE,{"disambiguationData":[TD([makeQuery(id+"F1.opRevolve","SWEPT_FACE",FACE,{"disambiguationData":[OSD([sQuery(id+"F0.wireOp",EDGE,"E8")])]})])],"derivedFrom":makeQuery(id+"F1.opRevolve","SWEPT_FACE",FACE,{"disambiguationData":[OSD([subQ0])]})}),makeQuery(id+"F13.opExtrude","SWEPT_FACE",FACE,{"disambiguationData":[OSD([sQuery(id+"F12.wireOp",EDGE,"E52"),sQuery(id+"F12.wireOp",EDGE,"E54")])]})]}),makeQuery(id+"F13.opExtrude","SWEPT_FACE",FACE,{"disambiguationData":[OSD([sQuery(id+"F12.wireOp",EDGE,"E45")])]})],"blendedInto":[makeQuery(id+"F13.opExtrude","SWEPT_FACE",FACE,{"disambiguationData":[OSD([sQuery(id+"F12.wireOp",EDGE,"E45")])]})]});}
            fillet(context, id + "F22", {"entities" : qUnion([Q0, Q1, Q2, Q3]), "radius" : 3.07 * mm, "tangentPropagation" : true, "allowEdgeOverflow" : false});
        }
        {
            var Q0;
            Q0=makeQuery(id+"F5.boolean.opBoolean","INTERSECT",EDGE,{"derivedFrom":[makeQuery(id+"F1.opRevolve","SWEPT_FACE",FACE,{"disambiguationData":[OSD([sQuery(id+"F0.wireOp",EDGE,"E2")])]}),makeQuery(id+"F5.opExtrude","SWEPT_FACE",FACE,{"disambiguationData":[OSD([sQuery(id+"F4.wireOp",EDGE,"E9.bottom"),sQuery(id+"F4.wireOp",EDGE,"E10"),sQuery(id+"F4.wireOp",EDGE,"E11")])]})]});
            var Q1;
            Q1=makeQuery(id+"F5.boolean.opBoolean","INTERSECT",EDGE,{"derivedFrom":[makeQuery(id+"F1.opRevolve","SWEPT_FACE",FACE,{"disambiguationData":[OSD([sQuery(id+"F0.wireOp",EDGE,"E2")])]}),makeQuery(id+"F5.opExtrude","SWEPT_FACE",FACE,{"disambiguationData":[OSD([sQuery(id+"F4.wireOp",EDGE,"E9.right")])]})]});
            var Q2;
            Q2=makeQuery(id+"F5.boolean.opBoolean","INTERSECT",EDGE,{"derivedFrom":[makeQuery(id+"F1.opRevolve","SWEPT_FACE",FACE,{"disambiguationData":[OSD([sQuery(id+"F0.wireOp",EDGE,"E2")])]}),makeQuery(id+"F5.opExtrude","SWEPT_FACE",FACE,{"disambiguationData":[OSD([sQuery(id+"F4.wireOp",EDGE,"E9.left")])]})]});
            var Q3;
            Q3=makeQuery(id+"F5.boolean.opBoolean","INTERSECT",EDGE,{"derivedFrom":[makeQuery(id+"F1.opRevolve","SWEPT_FACE",FACE,{"disambiguationData":[OSD([sQuery(id+"F0.wireOp",EDGE,"E2")])]}),makeQuery(id+"F5.opExtrude","SWEPT_FACE",FACE,{"disambiguationData":[OSD([sQuery(id+"F4.wireOp",EDGE,"E9.top")])]})]});
            fillet(context, id + "F23", {"entities" : qUnion([Q0, Q1, Q2, Q3]), "radius" : 4.83 * mm, "tangentPropagation" : true, "allowEdgeOverflow" : false});
        }
        {
            var Q0;
            Q0=makeQuery(id+"F18.opExtrude","CAP_EDGE",EDGE,{"disambiguationData":[OSD([sQuery(id+"F4.wireOp",EDGE,"E9.right")])],"isStart":false});
            var Q1;
            Q1=makeQuery(id+"F18.opExtrude","CAP_EDGE",EDGE,{"disambiguationData":[OSD([sQuery(id+"F4.wireOp",EDGE,"E9.bottom"),sQuery(id+"F4.wireOp",EDGE,"E10"),sQuery(id+"F4.wireOp",EDGE,"E11")])],"isStart":false});
            var Q2;
            Q2=makeQuery(id+"F18.opExtrude","CAP_EDGE",EDGE,{"disambiguationData":[OSD([sQuery(id+"F4.wireOp",EDGE,"E9.left")])],"isStart":false});
            var Q3;
            Q3=makeQuery(id+"F18.opExtrude","CAP_EDGE",EDGE,{"disambiguationData":[OSD([sQuery(id+"F4.wireOp",EDGE,"E9.top")])],"isStart":false});
            fillet(context, id + "F24", {"entities" : qUnion([Q0, Q1, Q2, Q3]), "radius" : 1 * mm, "tangentPropagation" : true, "allowEdgeOverflow" : false});
        }
    });
